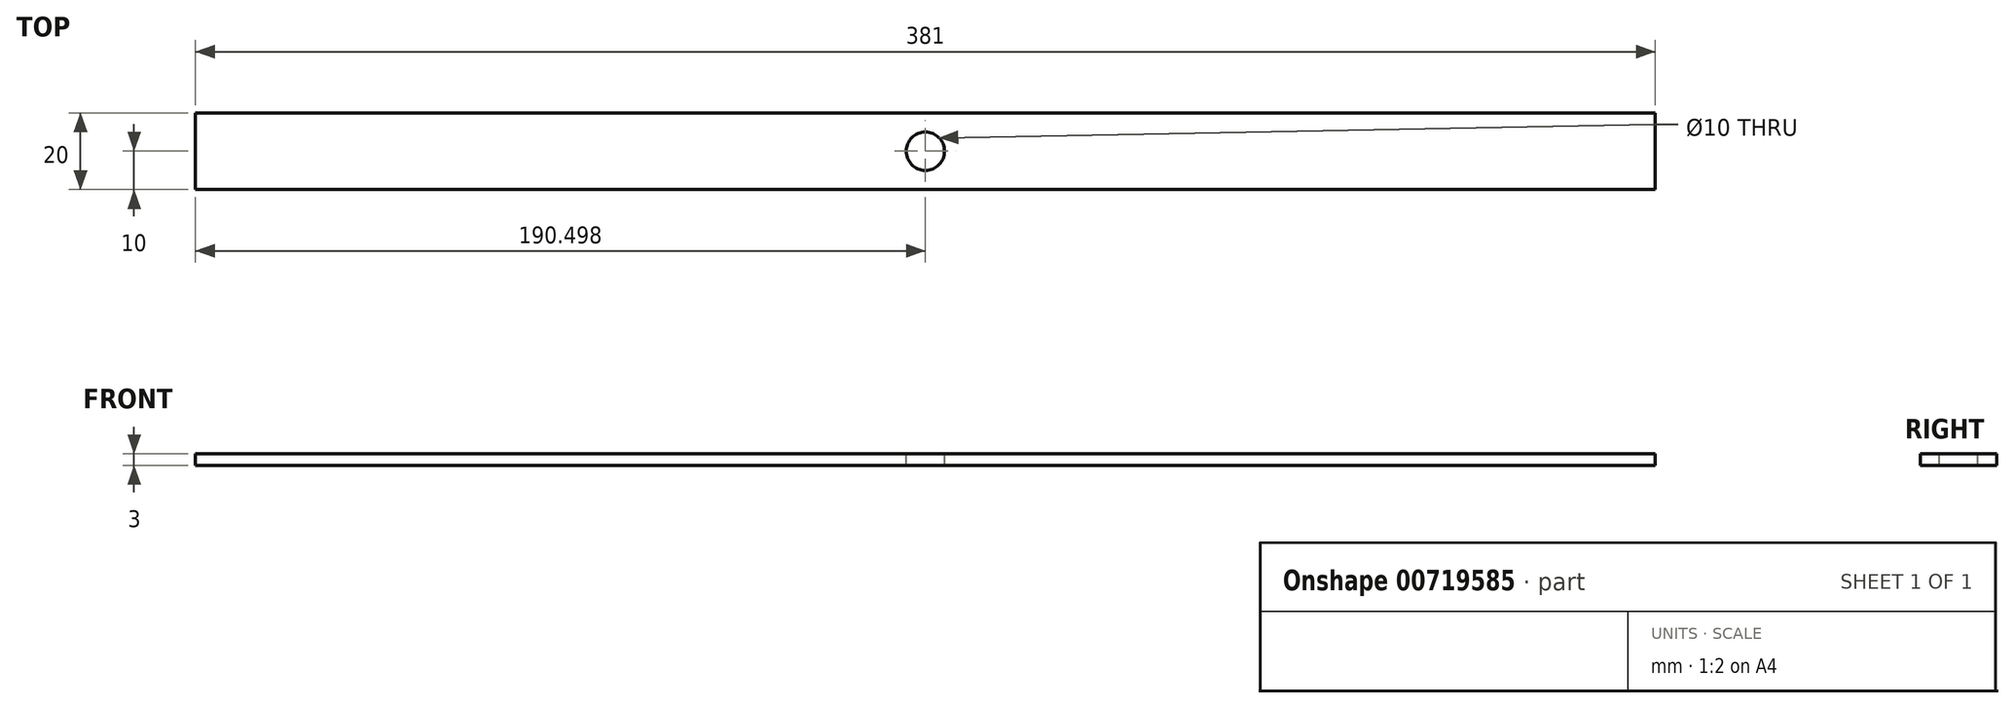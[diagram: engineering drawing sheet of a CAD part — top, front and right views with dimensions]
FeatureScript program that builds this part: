
annotation { "Feature Type Name" : "Feature", "Feature Type Description" : "" }
export const myFeature = defineFeature(function(context is Context, id is Id, definition is map)
    precondition{}
    {
        {
            var Q0;
            Q0=qCreatedBy(makeId("Top.planeOp"),FACE);
            var sketch = newSketch(context, id + "F0", { "sketchPlane" : qUnion([Q0])});
            skLineSegment(sketch, "E0.bottom", {"start": v(323.32, -7.41) * mm, "end": v(-57.68, -7.41) * mm});
            skLineSegment(sketch, "E0.top", {"start": v(323.32, 12.59) * mm, "end": v(-57.68, 12.59) * mm});
            skLineSegment(sketch, "E0.left", {"start": v(323.32, -7.41) * mm, "end": v(323.32, 12.59) * mm});
            skLineSegment(sketch, "E0.right", {"start": v(-57.68, -7.41) * mm, "end": v(-57.68, 12.59) * mm});
            skSolve(sketch);
        }
        {
            var Q0;
            Q0=makeQuery(id+"F0.imprint","IMPRINT",FACE,{"disambiguationData":[TD([[makeQuery(id+"F0.imprint","IMPRINT",EDGE,{"derivedFrom":sQuery(id+"F0.wireOp",EDGE,"E0.bottom")}),-1.0]])]});
            extrude(context, id + "F1", {"entities" : qUnion([Q0]), "depth" : 3 * mm, "offsetDistance" : 25 * mm});
        }
        {
            var Q0;
            Q0=makeQuery(id+"F1.opExtrude","CAP_FACE",FACE,{"disambiguationData":[OSD([sQuery(id+"F0.wireOp",EDGE,"E0.bottom"),sQuery(id+"F0.wireOp",EDGE,"E0.top"),sQuery(id+"F0.wireOp",EDGE,"E0.left"),sQuery(id+"F0.wireOp",EDGE,"E0.right")])],"isStart":false});
            var sketch = newSketch(context, id + "F2", { "sketchPlane" : qUnion([Q0])});
            skLineSegment(sketch, "E1", {"start": v(132.82, -2.41) * mm, "end": v(132.82, 7.59) * mm});
            skLineSegment(sketch, "E2", {"start": v(92.82, 2.59) * mm, "end": v(132.82, 2.59) * mm});
            skPoint(sketch, "E2.startSnap0", {"position": v(132.82, 2.59) * mm});
            skLineSegment(sketch, "E3.MirrorCS", {"start": v(172.82, 2.59) * mm, "end": v(132.82, 2.59) * mm});
            skCircle(sketch, "E4", {"center": v(132.82, 2.59) * mm, "radius": 5 * mm});
            skPoint(sketch, "E5.orphan", {"position": v(132.82, 12.59) * mm});
            skPoint(sketch, "E6.orphan", {"position": v(132.82, -7.41) * mm});
            skSolve(sketch);
        }
        {
            var Q0;
            {var subQ0=sQuery(id+"F2.wireOp",EDGE,"E3.MirrorCS");var subQ3=sQuery(id+"F2.wireOp",EDGE,"E4");var subQ5=makeQuery(id+"F2.imprint","INTERSECT",VERTEX,{"derivedFrom":[subQ0,subQ3]});Q0=makeQuery(id+"F2.imprint","IMPRINT",FACE,{"disambiguationData":[TD([[makeQuery(id+"F2.imprint","IMPRINT",EDGE,{"disambiguationData":[TD([[subQ5,-1.0]])],"derivedFrom":subQ3}),1.0]])]});}
            var Q1;
            {var subQ0=sQuery(id+"F2.wireOp",EDGE,"E2");var subQ3=sQuery(id+"F2.wireOp",EDGE,"E4");var subQ5=makeQuery(id+"F2.imprint","INTERSECT",VERTEX,{"derivedFrom":[subQ0,subQ3]});Q1=makeQuery(id+"F2.imprint","IMPRINT",FACE,{"disambiguationData":[TD([[makeQuery(id+"F2.imprint","IMPRINT",EDGE,{"disambiguationData":[TD([[subQ5,1.0]])],"derivedFrom":subQ3}),1.0]])]});}
            var Q2;
            {var subQ0=sQuery(id+"F2.wireOp",EDGE,"E2");var subQ3=sQuery(id+"F2.wireOp",EDGE,"E4");var subQ5=makeQuery(id+"F2.imprint","INTERSECT",VERTEX,{"derivedFrom":[subQ0,subQ3]});Q2=makeQuery(id+"F2.imprint","IMPRINT",FACE,{"disambiguationData":[TD([[makeQuery(id+"F2.imprint","IMPRINT",EDGE,{"disambiguationData":[TD([[subQ5,-1.0]])],"derivedFrom":subQ3}),1.0]])]});}
            var Q3;
            {var subQ0=sQuery(id+"F2.wireOp",EDGE,"E3.MirrorCS");var subQ3=sQuery(id+"F2.wireOp",EDGE,"E4");var subQ5=makeQuery(id+"F2.imprint","INTERSECT",VERTEX,{"derivedFrom":[subQ0,subQ3]});Q3=makeQuery(id+"F2.imprint","IMPRINT",FACE,{"disambiguationData":[TD([[makeQuery(id+"F2.imprint","IMPRINT",EDGE,{"disambiguationData":[TD([[subQ5,1.0]])],"derivedFrom":subQ3}),1.0]])]});}
            var Q4;
            Q4=sQuery(id+"F2.wireOp",EDGE,"E4");
            extrude(context, id + "F3", {"entities" : qUnion([Q0, Q1, Q2, Q3]), "operationType" : NewBodyOperationType.REMOVE, "surfaceEntities" : qUnion([Q4]), "oppositeDirection" : true, "depth" : 25 * mm, "offsetDistance" : 25 * mm});
        }
    });
